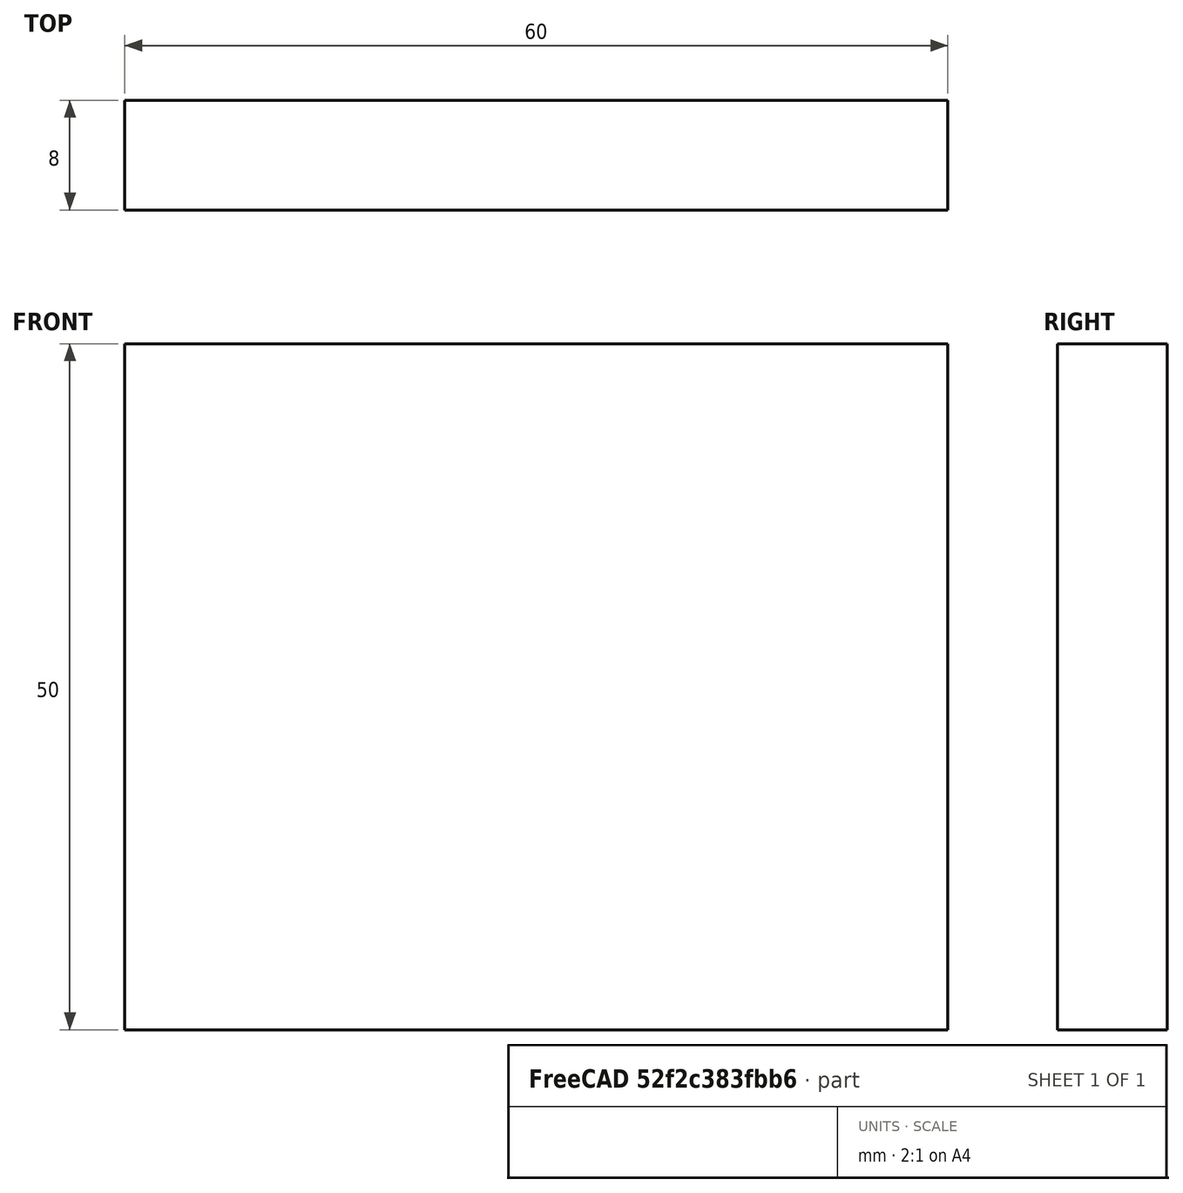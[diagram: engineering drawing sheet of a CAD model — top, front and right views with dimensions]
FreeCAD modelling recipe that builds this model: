
FCSTD DOCUMENT  (FreeCAD 0.15R4671 (Git))
Label: Flat Bar 60x8 EN10058 S235JR
License: All rights reserved
LicenseURL: http://en.wikipedia.org/wiki/All_rights_reserved
objects: Sketcher::SketchObject×1, Part::Extrusion×1
note: 2 computed .brp shape members not serialized (recipe doc carries the construction recipe); baked Part::Feature solids carry a one-line shape summary decoded from their .brp

FEATURE [Sketcher::SketchObject] Sketch
  sketch-geometry (4):
    g0: LineSegment StartX=-30 StartY=-4 StartZ=0 EndX=30 EndY=-4 EndZ=0
    g1: LineSegment StartX=30 StartY=-4 StartZ=0 EndX=30 EndY=4 EndZ=0
    g2: LineSegment StartX=30 StartY=4 StartZ=0 EndX=-30 EndY=4 EndZ=0
    g3: LineSegment StartX=-30 StartY=4 StartZ=0 EndX=-30 EndY=-4 EndZ=0
  constraints (12):
    c: Coincident(g0,g1)
    c: Coincident(g1,g2)
    c: Coincident(g2,g3)
    c: Coincident(g3,g0)
    c: Horizontal(g0)
    c: Horizontal(g2)
    c: Vertical(g1)
    c: Vertical(g3)
    c: Symmetric(g1,g2,g-2)
    c: Symmetric(g0,g1,g-1)
    c: DistanceY(g1) = 8
    c: DistanceX(g0) = 60
FEATURE [Part::Extrusion] Extrude  label="Flat Bar 60x8 EN10058 S235JR"
  Base = -> Sketch
  Dir = (0,0,50)
  Solid = true
